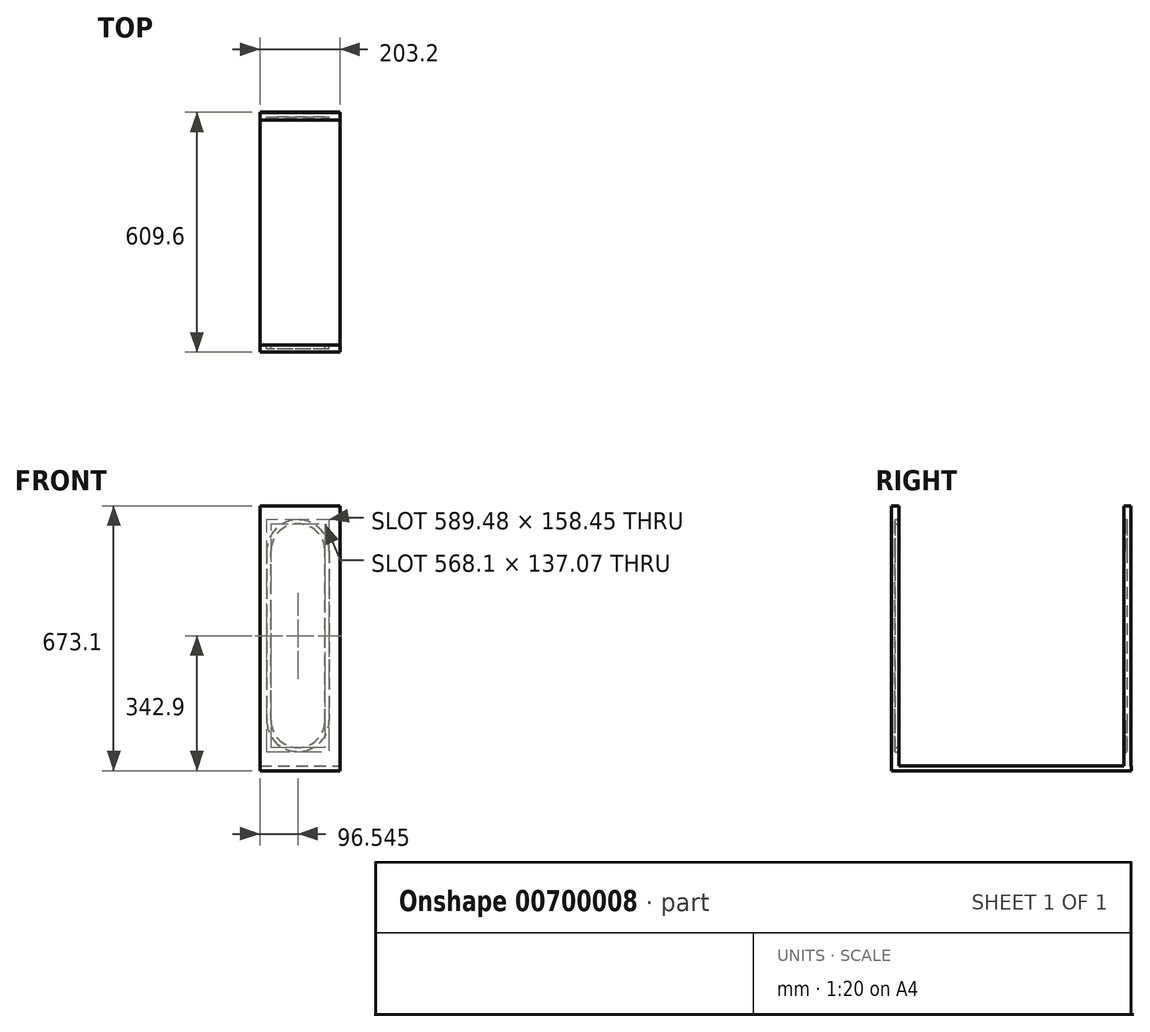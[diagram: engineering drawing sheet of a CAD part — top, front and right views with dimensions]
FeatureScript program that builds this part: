
annotation { "Feature Type Name" : "Feature", "Feature Type Description" : "" }
export const myFeature = defineFeature(function(context is Context, id is Id, definition is map)
    precondition{}
    {
        {
            var Q0;
            Q0=qCreatedBy(makeId("Top.planeOp"),FACE);
            var sketch = newSketch(context, id + "F0", { "sketchPlane" : qUnion([Q0])});
            skLineSegment(sketch, "E0.bottom", {"start": v(-128.38, 305.32) * mm, "end": v(74.82, 305.32) * mm});
            skLineSegment(sketch, "E0.top", {"start": v(-128.38, -304.28) * mm, "end": v(74.82, -304.28) * mm});
            skLineSegment(sketch, "E0.left", {"start": v(-128.38, 305.32) * mm, "end": v(-128.38, -304.28) * mm});
            skLineSegment(sketch, "E0.right", {"start": v(74.82, 305.32) * mm, "end": v(74.82, -304.28) * mm});
            skSolve(sketch);
        }
        {
            var Q0;
            Q0=makeQuery(id+"F0.imprint","IMPRINT",FACE,{"disambiguationData":[TD([[makeQuery(id+"F0.imprint","IMPRINT",EDGE,{"derivedFrom":sQuery(id+"F0.wireOp",EDGE,"E0.bottom")}),-1.0]])]});
            extrude(context, id + "F1", {"entities" : qUnion([Q0]), "depth" : 12.7 * mm, "offsetDistance" : 25.4 * mm});
        }
        {
            var Q0;
            Q0=makeQuery(id+"F1.opExtrude","CAP_FACE",FACE,{"disambiguationData":[OSD([sQuery(id+"F0.wireOp",EDGE,"E0.bottom"),sQuery(id+"F0.wireOp",EDGE,"E0.top"),sQuery(id+"F0.wireOp",EDGE,"E0.left"),sQuery(id+"F0.wireOp",EDGE,"E0.right")])],"isStart":false});
            var sketch = newSketch(context, id + "F2", { "sketchPlane" : qUnion([Q0])});
            skLineSegment(sketch, "E1.bottom", {"start": v(-128.38, -285.53) * mm, "end": v(74.82, -285.53) * mm});
            skLineSegment(sketch, "E1.top", {"start": v(-128.38, -304.28) * mm, "end": v(74.82, -304.28) * mm});
            skLineSegment(sketch, "E1.left", {"start": v(-128.38, -285.53) * mm, "end": v(-128.38, -304.28) * mm});
            skLineSegment(sketch, "E1.right", {"start": v(74.82, -285.53) * mm, "end": v(74.82, -304.28) * mm});
            skLineSegment(sketch, "E2", {"start": v(74.82, 0) * mm, "end": v(-244.04, 0) * mm, "construction": true});
            skLineSegment(sketch, "E3.MirrorCS", {"start": v(-128.38, 285.53) * mm, "end": v(74.82, 285.53) * mm});
            skLineSegment(sketch, "E4.MirrorCS", {"start": v(-128.38, 304.28) * mm, "end": v(74.82, 304.28) * mm});
            skLineSegment(sketch, "E5.MirrorCS", {"start": v(74.82, 285.53) * mm, "end": v(74.82, 304.28) * mm});
            skLineSegment(sketch, "E6.MirrorCS", {"start": v(-128.38, 285.53) * mm, "end": v(-128.38, 304.28) * mm});
            skSolve(sketch);
        }
        {
            var Q0;
            Q0=makeQuery(id+"F2.imprint","IMPRINT",FACE,{"disambiguationData":[TD([[makeQuery(id+"F2.imprint","IMPRINT",EDGE,{"derivedFrom":sQuery(id+"F2.wireOp",EDGE,"E3.MirrorCS")}),1.0]])]});
            var Q1;
            Q1=makeQuery(id+"F2.imprint","IMPRINT",FACE,{"disambiguationData":[TD([[makeQuery(id+"F2.imprint","IMPRINT",EDGE,{"derivedFrom":sQuery(id+"F2.wireOp",EDGE,"E1.bottom")}),-1.0]])]});
            extrude(context, id + "F3", {"entities" : qUnion([Q0, Q1]), "operationType" : NewBodyOperationType.ADD, "depth" : 660.4 * mm, "offsetDistance" : 25.4 * mm});
        }
        {
            var Q0;
            Q0=makeQuery(id+"F3.opExtrude","SWEPT_FACE",FACE,{"disambiguationData":[OSD([sQuery(id+"F2.wireOp",EDGE,"E1.bottom")])]});
            var sketch = newSketch(context, id + "F4", { "sketchPlane" : qUnion([Q0])});
            skArc(sketch, "E7", {"start": v(-47.4, 127.48) * mm, "mid": v(31.85, 48.16) * mm, "end": v(111.06, 127.5) * mm});
            skArc(sketch, "E8", {"start": v(-36.7, 127.48) * mm, "mid": v(31.85, 58.85) * mm, "end": v(100.37, 127.5) * mm});
            skLineSegment(sketch, "E9", {"start": v(128.38, 342.9) * mm, "end": v(-74.82, 342.9) * mm, "construction": true});
            skArc(sketch, "E10.MirrorC", {"start": v(-36.7, 558.32) * mm, "mid": v(31.85, 626.95) * mm, "end": v(100.37, 558.3) * mm});
            skArc(sketch, "E11.MirrorC", {"start": v(-47.4, 558.32) * mm, "mid": v(31.85, 637.64) * mm, "end": v(111.06, 558.3) * mm});
            skLineSegment(sketch, "E12.left", {"start": v(-47.4, 558.5) * mm, "end": v(-47.4, 127.28) * mm});
            skLineSegment(sketch, "E12.right", {"start": v(111.06, 558.5) * mm, "end": v(111.06, 127.28) * mm});
            skLineSegment(sketch, "E13.left", {"start": v(100.37, 127.28) * mm, "end": v(100.37, 558.5) * mm});
            skLineSegment(sketch, "E13.right", {"start": v(-36.7, 127.28) * mm, "end": v(-36.7, 558.5) * mm});
            skSolve(sketch);
        }
        {
            var Q0;
            Q0 = qSketchRegion(id + "F4", true);
            extrude(context, id + "F5", {"entities" : qUnion([Q0]), "operationType" : NewBodyOperationType.REMOVE, "oppositeDirection" : true, "depth" : 10.16 * mm, "offsetDistance" : 25.4 * mm, "hasSecondDirection" : true, "secondDirectionOppositeDirection" : false, "secondDirectionDepth" : 579.12 * mm});
        }
    });
